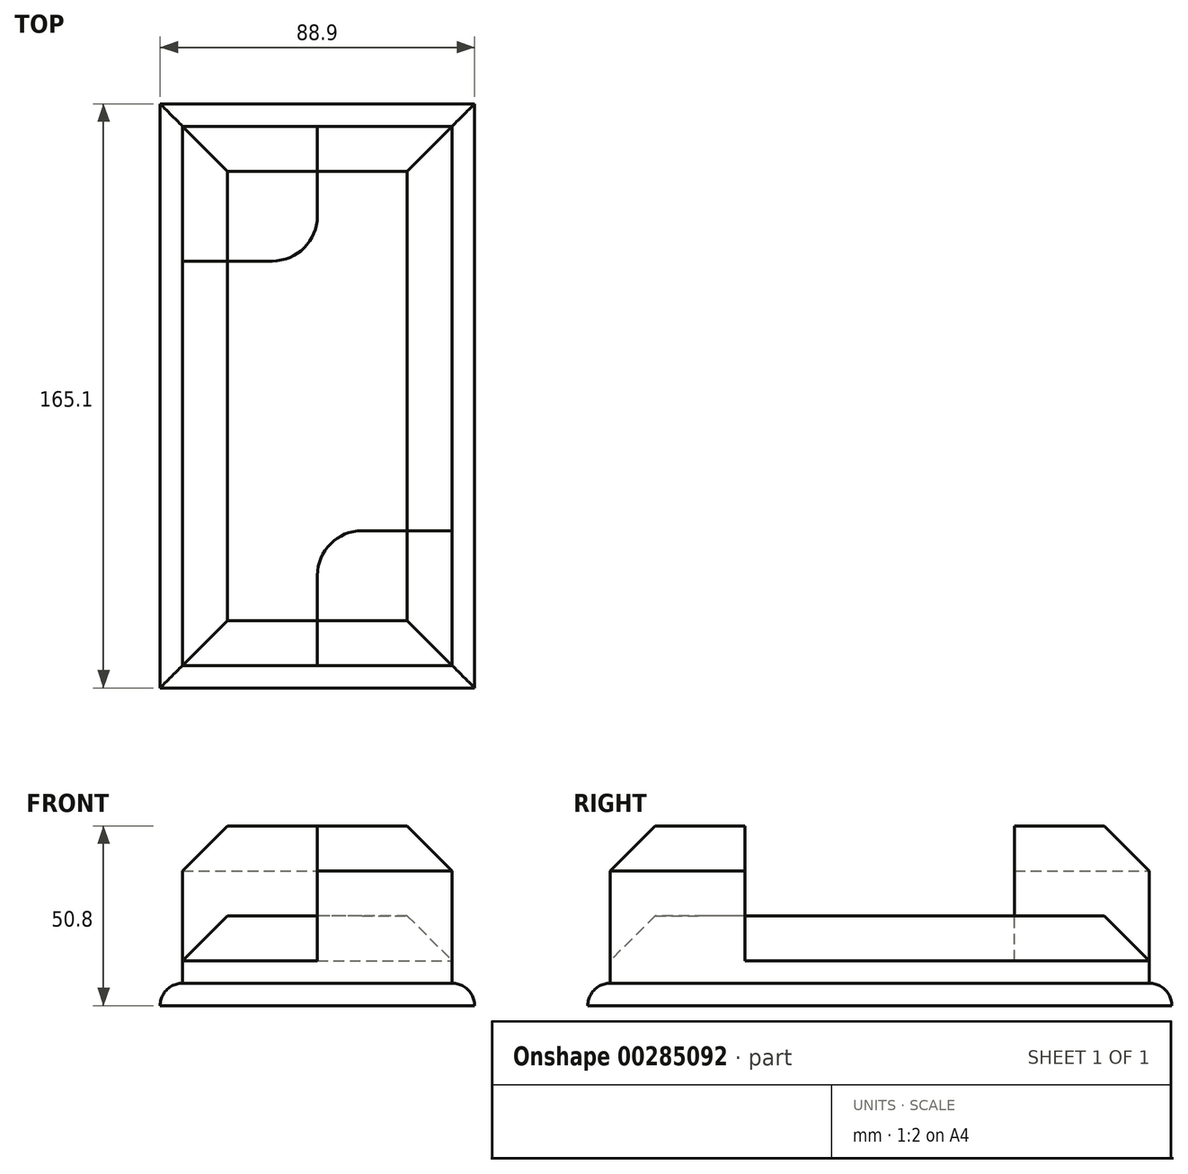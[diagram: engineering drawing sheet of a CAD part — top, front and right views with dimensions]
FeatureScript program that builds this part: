
annotation { "Feature Type Name" : "Feature", "Feature Type Description" : "" }
export const myFeature = defineFeature(function(context is Context, id is Id, definition is map)
    precondition{}
    {
        {
            var Q0;
            Q0=qCreatedBy(makeId("Top.planeOp"),FACE);
            var sketch = newSketch(context, id + "F0", { "sketchPlane" : qUnion([Q0])});
            skLineSegment(sketch, "E0.bottom", {"start": v(-39.92, 79.29) * mm, "end": v(36.28, 79.29) * mm});
            skLineSegment(sketch, "E0.top", {"start": v(-39.92, -73.11) * mm, "end": v(36.28, -73.11) * mm});
            skLineSegment(sketch, "E0.left", {"start": v(-39.92, 79.29) * mm, "end": v(-39.92, -73.11) * mm});
            skLineSegment(sketch, "E0.right", {"start": v(36.28, 79.29) * mm, "end": v(36.28, -73.11) * mm});
            skLineSegment(sketch, "E1.0", {"start": v(-46.27, 85.64) * mm, "end": v(-46.27, -79.46) * mm});
            skLineSegment(sketch, "E1.1", {"start": v(-46.27, 85.64) * mm, "end": v(42.63, 85.64) * mm});
            skLineSegment(sketch, "E1.2", {"start": v(42.63, 85.64) * mm, "end": v(42.63, -79.46) * mm});
            skLineSegment(sketch, "E1.3", {"start": v(-46.27, -79.46) * mm, "end": v(42.63, -79.46) * mm});
            skLineSegment(sketch, "E2", {"start": v(-1.82, 79.29) * mm, "end": v(-1.82, 53.89) * mm});
            skLineSegment(sketch, "E3", {"start": v(-14.52, 41.19) * mm, "end": v(-39.92, 41.19) * mm});
            skLineSegment(sketch, "E4", {"start": v(-1.82, -73.11) * mm, "end": v(-1.82, -47.71) * mm});
            skLineSegment(sketch, "E5", {"start": v(10.88, -35.01) * mm, "end": v(36.28, -35.01) * mm});
            skPoint(sketch, "E6.visualSharp", {"position": v(-1.82, 41.19) * mm});
            skArc(sketch, "E6.filletArc", {"start": v(-14.52, 41.19) * mm, "mid": v(-5.54, 44.9) * mm, "end": v(-1.82, 53.89) * mm});
            skPoint(sketch, "E7.visualSharp", {"position": v(-1.82, -35.01) * mm});
            skArc(sketch, "E7.filletArc", {"start": v(10.88, -35.01) * mm, "mid": v(1.9, -38.73) * mm, "end": v(-1.82, -47.71) * mm});
            skSolve(sketch);
        }
        {
            var Q0;
            Q0=makeQuery(id+"F0.imprint","IMPRINT",FACE,{"disambiguationData":[TD([[makeQuery(id+"F0.imprint","IMPRINT",EDGE,{"derivedFrom":sQuery(id+"F0.wireOp",EDGE,"E1.0")}),1.0]])]});
            extrude(context, id + "F1", {"entities" : qUnion([Q0]), "depth" : 6.35 * mm});
        }
        {
            var Q0;
            {var subQ9=sQuery(id+"F0.wireOp",EDGE,"E2");Q0=makeQuery(id+"F0.imprint","IMPRINT",FACE,{"disambiguationData":[TD([[makeQuery(id+"F0.imprint","IMPRINT",EDGE,{"derivedFrom":subQ9}),1.0]])]});}
            extrude(context, id + "F2", {"entities" : qUnion([Q0]), "operationType" : NewBodyOperationType.ADD, "depth" : 25.4 * mm});
        }
        {
            var Q0;
            {var subQ1=sQuery(id+"F0.wireOp",EDGE,"E2");Q0=makeQuery(id+"F0.imprint","IMPRINT",FACE,{"disambiguationData":[TD([[makeQuery(id+"F0.imprint","IMPRINT",EDGE,{"derivedFrom":subQ1}),-1.0]])]});}
            var Q1;
            {var subQ1=sQuery(id+"F0.wireOp",EDGE,"E4");Q1=makeQuery(id+"F0.imprint","IMPRINT",FACE,{"disambiguationData":[TD([[makeQuery(id+"F0.imprint","IMPRINT",EDGE,{"derivedFrom":subQ1}),-1.0]])]});}
            extrude(context, id + "F3", {"entities" : qUnion([Q0, Q1]), "operationType" : NewBodyOperationType.ADD, "depth" : 50.8 * mm});
        }
        {
            var Q0;
            Q0=makeQuery(id+"F1.opExtrude","CAP_EDGE",EDGE,{"disambiguationData":[OSD([sQuery(id+"F0.wireOp",EDGE,"E1.0")])],"isStart":false});
            var Q1;
            Q1=makeQuery(id+"F1.opExtrude","CAP_EDGE",EDGE,{"disambiguationData":[OSD([sQuery(id+"F0.wireOp",EDGE,"E1.3")])],"isStart":false});
            var Q2;
            Q2=makeQuery(id+"F1.opExtrude","CAP_EDGE",EDGE,{"disambiguationData":[OSD([sQuery(id+"F0.wireOp",EDGE,"E1.2")])],"isStart":false});
            var Q3;
            Q3=makeQuery(id+"F1.opExtrude","CAP_EDGE",EDGE,{"disambiguationData":[OSD([sQuery(id+"F0.wireOp",EDGE,"E1.1")])],"isStart":false});
            fillet(context, id + "F4", {"entities" : qUnion([Q0, Q1, Q2, Q3]), "radius" : 6.35 * mm, "tangentPropagation" : true, "allowEdgeOverflow" : false});
        }
        {
            var Q0;
            Q0=makeQuery(id+"F3.opExtrude","CAP_EDGE",EDGE,{"disambiguationData":[OSD([sQuery(id+"F0.wireOp",EDGE,"E0.top")])],"isStart":false});
            var Q1;
            Q1=makeQuery(id+"F3.opExtrude","CAP_EDGE",EDGE,{"disambiguationData":[OSD([sQuery(id+"F0.wireOp",EDGE,"E0.right")])],"isStart":false});
            var Q2;
            Q2=makeQuery(id+"F3.opExtrude","CAP_EDGE",EDGE,{"disambiguationData":[OSD([sQuery(id+"F0.wireOp",EDGE,"E0.left")])],"isStart":false});
            var Q3;
            Q3=makeQuery(id+"F3.opExtrude","CAP_EDGE",EDGE,{"disambiguationData":[OSD([sQuery(id+"F0.wireOp",EDGE,"E0.bottom")])],"isStart":false});
            var Q4;
            Q4=makeQuery(id+"F2.opExtrude","CAP_EDGE",EDGE,{"disambiguationData":[OSD([sQuery(id+"F0.wireOp",EDGE,"E0.left")])],"isStart":false});
            var Q5;
            Q5=makeQuery(id+"F2.opExtrude","CAP_EDGE",EDGE,{"disambiguationData":[OSD([sQuery(id+"F0.wireOp",EDGE,"E0.top")])],"isStart":false});
            var Q6;
            Q6=makeQuery(id+"F2.opExtrude","CAP_EDGE",EDGE,{"disambiguationData":[OSD([sQuery(id+"F0.wireOp",EDGE,"E0.right")])],"isStart":false});
            var Q7;
            Q7=makeQuery(id+"F2.opExtrude","CAP_EDGE",EDGE,{"disambiguationData":[OSD([sQuery(id+"F0.wireOp",EDGE,"E0.bottom")])],"isStart":false});
            chamfer(context, id + "F5", {"entities" : qUnion([Q0, Q1, Q2, Q3, Q4, Q5, Q6, Q7]), "width" : 12.7 * mm, "tangentPropagation" : true});
        }
    });
